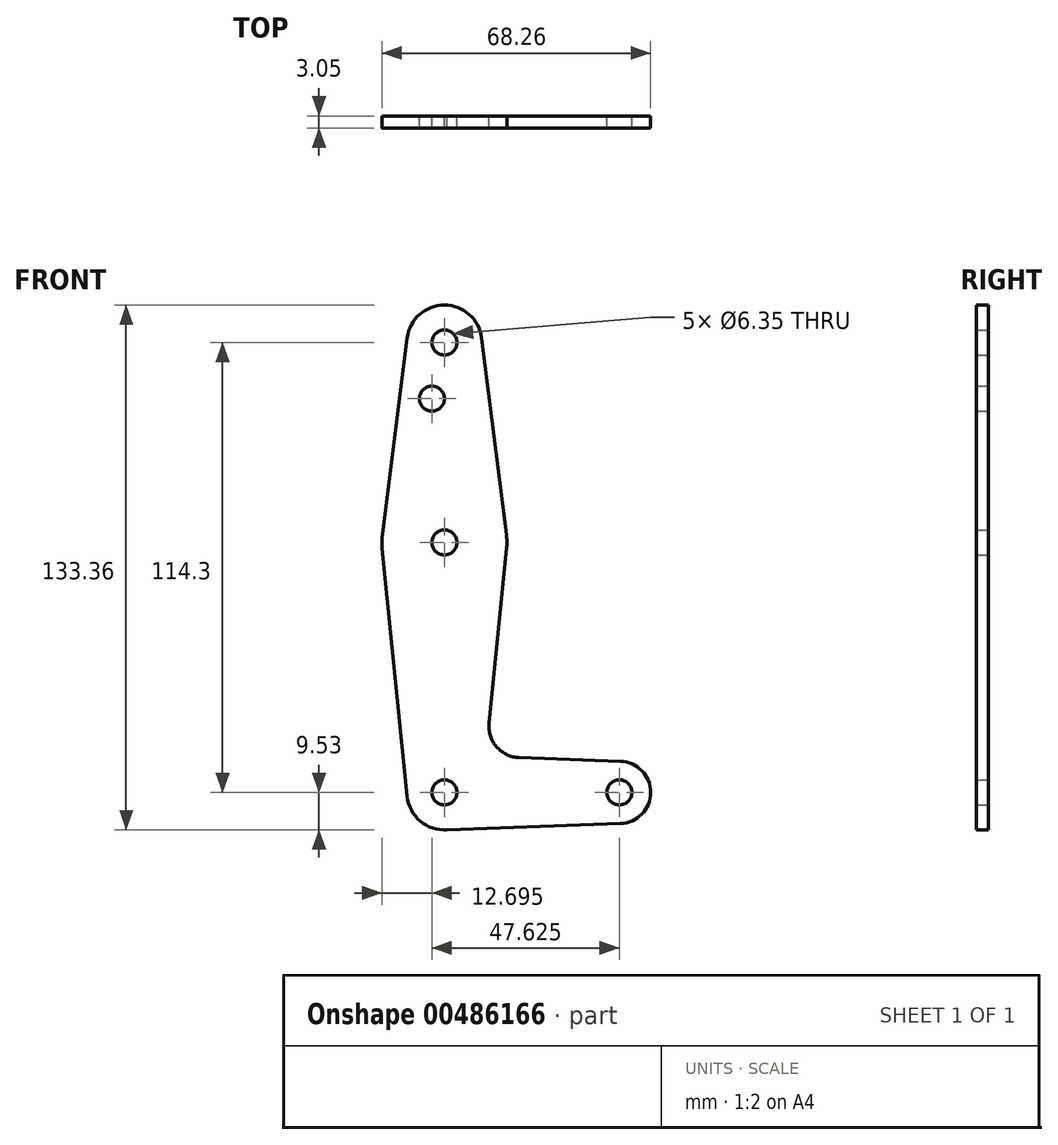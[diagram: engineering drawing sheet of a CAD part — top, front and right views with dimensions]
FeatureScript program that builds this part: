
annotation { "Feature Type Name" : "Feature", "Feature Type Description" : "" }
export const myFeature = defineFeature(function(context is Context, id is Id, definition is map)
    precondition{}
    {
        {
            var Q0;
            Q0=qCreatedBy(makeId("Front.planeOp"),FACE);
            var sketch = newSketch(context, id + "F0", { "sketchPlane" : qUnion([Q0])});
            skLineSegment(sketch, "E0", {"start": v(0, 114.3) * mm, "end": v(0, 0) * mm, "construction": true});
            skLineSegment(sketch, "E1", {"start": v(44.45, 0) * mm, "end": v(0, 0) * mm, "construction": true});
            skCircle(sketch, "E2", {"center": v(0, 114.3) * mm, "radius": 9.52 * mm});
            skCircle(sketch, "E3", {"center": v(44.45, 0) * mm, "radius": 7.94 * mm});
            skCircle(sketch, "E4", {"center": v(0, 0) * mm, "radius": 9.53 * mm});
            skCircle(sketch, "E5", {"center": v(0, 63.5) * mm, "radius": 15.88 * mm});
            skLineSegment(sketch, "E6", {"start": v(9.45, 115.5) * mm, "end": v(15.75, 65.48) * mm});
            skLineSegment(sketch, "E7", {"start": v(-9.45, 115.5) * mm, "end": v(-15.75, 65.48) * mm});
            skLineSegment(sketch, "E8", {"start": v(18.97, 8.85) * mm, "end": v(44.73, 7.93) * mm});
            skLineSegment(sketch, "E9", {"start": v(0, -9.53) * mm, "end": v(44.73, -7.93) * mm});
            skLineSegment(sketch, "E10", {"start": v(-15.8, 61.91) * mm, "end": v(-9.48, -0.95) * mm});
            skLineSegment(sketch, "E11", {"start": v(15.8, 61.91) * mm, "end": v(11.34, 17.59) * mm});
            skCircle(sketch, "E12", {"center": v(0, 114.3) * mm, "radius": 3.18 * mm});
            skCircle(sketch, "E13", {"center": v(0, 0) * mm, "radius": 3.18 * mm});
            skCircle(sketch, "E14", {"center": v(44.45, 0) * mm, "radius": 3.18 * mm});
            skCircle(sketch, "E15", {"center": v(0, 63.5) * mm, "radius": 3.18 * mm});
            skCircle(sketch, "E16", {"center": v(-3.17, 100.03) * mm, "radius": 3.18 * mm});
            skArc(sketch, "E17.filletArc", {"start": v(11.34, 17.59) * mm, "mid": v(13.26, 11.57) * mm, "end": v(18.97, 8.85) * mm});
            skSolve(sketch);
        }
        {
            var Q0;
            Q0 = qSketchRegion(id + "F0", true);
            extrude(context, id + "F1", {"entities" : qUnion([Q0]), "depth" : 3.05 * mm});
        }
    });
